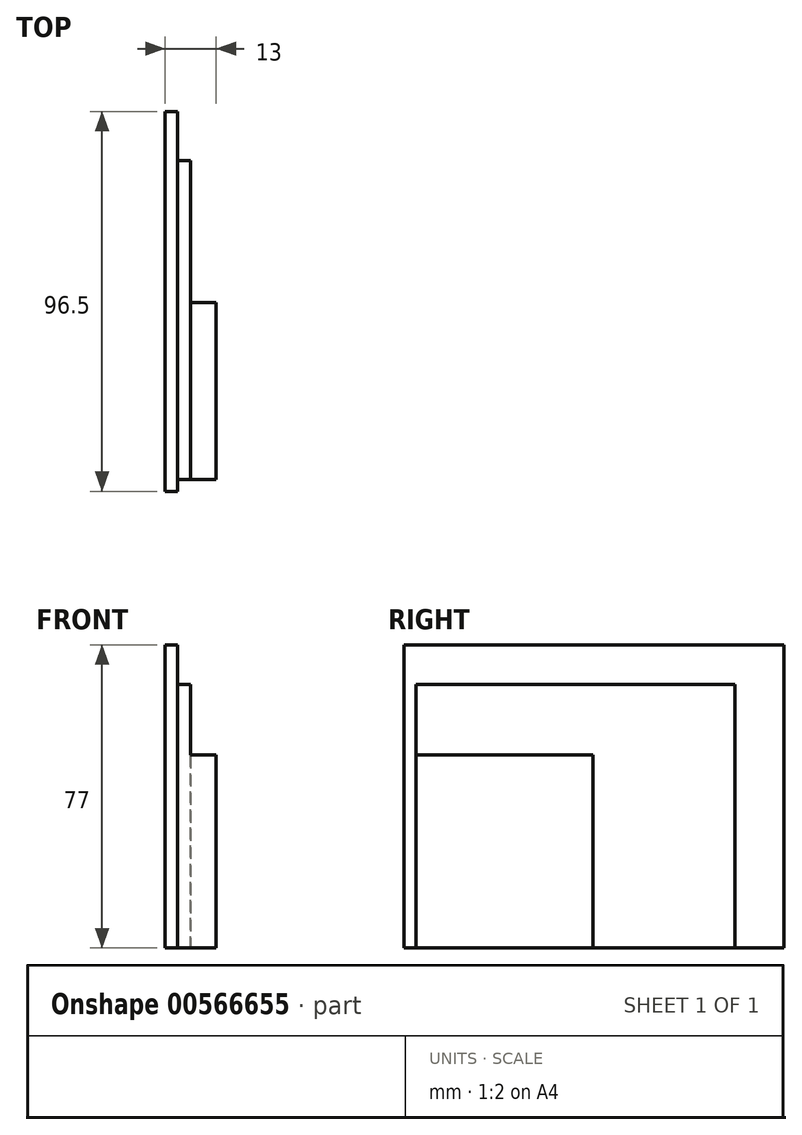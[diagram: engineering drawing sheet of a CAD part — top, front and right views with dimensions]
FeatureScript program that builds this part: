
annotation { "Feature Type Name" : "Feature", "Feature Type Description" : "" }
export const myFeature = defineFeature(function(context is Context, id is Id, definition is map)
    precondition{}
    {
        {
            var Q0;
            Q0=qCreatedBy(makeId("Right.planeOp"),FACE);
            var sketch = newSketch(context, id + "F0", { "sketchPlane" : qUnion([Q0])});
            skLineSegment(sketch, "E0.bottom", {"start": v(-48.25, 38.5) * mm, "end": v(48.25, 38.5) * mm});
            skLineSegment(sketch, "E0.top", {"start": v(-48.25, -38.5) * mm, "end": v(48.25, -38.5) * mm});
            skLineSegment(sketch, "E0.left", {"start": v(-48.25, 38.5) * mm, "end": v(-48.25, -38.5) * mm});
            skLineSegment(sketch, "E0.right", {"start": v(48.25, 38.5) * mm, "end": v(48.25, -38.5) * mm});
            skPoint(sketch, "E0.middle", {"position": v(0, 0) * mm});
            skSolve(sketch);
        }
        {
            var Q0;
            Q0=qSketchRegion(id+"F0",true);
            extrude(context, id + "F1", {"entities" : qUnion([Q0]), "endBound" : BoundingType.SYMMETRIC, "depth" : 3.2 * mm, "offsetDistance" : 25 * mm});
        }
        {
            var Q0;
            Q0=makeQuery(id+"F1.opExtrude","CAP_FACE",FACE,{"disambiguationData":[OSD([sQuery(id+"F0.wireOp",EDGE,"E0.bottom"),sQuery(id+"F0.wireOp",EDGE,"E0.top"),sQuery(id+"F0.wireOp",EDGE,"E0.left"),sQuery(id+"F0.wireOp",EDGE,"E0.right")])],"isStart":false});
            var sketch = newSketch(context, id + "F2", { "sketchPlane" : qUnion([Q0])});
            skLineSegment(sketch, "E1.bottom", {"start": v(-45.25, 28.5) * mm, "end": v(35.75, 28.5) * mm});
            skLineSegment(sketch, "E1.top", {"start": v(-45.25, -38.5) * mm, "end": v(35.75, -38.5) * mm});
            skLineSegment(sketch, "E1.left", {"start": v(-45.25, 28.5) * mm, "end": v(-45.25, -38.5) * mm});
            skLineSegment(sketch, "E1.right", {"start": v(35.75, 28.5) * mm, "end": v(35.75, -38.5) * mm});
            skSolve(sketch);
        }
        {
            var Q0;
            Q0=makeQuery(id+"F2.imprint","IMPRINT",FACE,{"disambiguationData":[TD([[makeQuery(id+"F2.imprint","IMPRINT",EDGE,{"derivedFrom":sQuery(id+"F2.wireOp",EDGE,"E1.bottom")}),-1.0]])]});
            extrude(context, id + "F3", {"entities" : qUnion([Q0]), "operationType" : NewBodyOperationType.ADD, "depth" : 3.3 * mm, "offsetDistance" : 25 * mm});
        }
        {
            var Q0;
            Q0=makeQuery(id+"F3.opExtrude","CAP_FACE",FACE,{"disambiguationData":[OSD([sQuery(id+"F2.wireOp",EDGE,"E1.bottom"),sQuery(id+"F2.wireOp",EDGE,"E1.top"),sQuery(id+"F2.wireOp",EDGE,"E1.left"),sQuery(id+"F2.wireOp",EDGE,"E1.right")])],"isStart":false});
            var sketch = newSketch(context, id + "F4", { "sketchPlane" : qUnion([Q0])});
            skLineSegment(sketch, "E2.bottom", {"start": v(-45.25, -38.5) * mm, "end": v(-0.25, -38.5) * mm});
            skLineSegment(sketch, "E2.top", {"start": v(-45.25, 10.5) * mm, "end": v(-0.25, 10.5) * mm});
            skLineSegment(sketch, "E2.left", {"start": v(-45.25, -38.5) * mm, "end": v(-45.25, 10.5) * mm});
            skLineSegment(sketch, "E2.right", {"start": v(-0.25, -38.5) * mm, "end": v(-0.25, 10.5) * mm});
            skSolve(sketch);
        }
        {
            var Q0;
            Q0=qSketchRegion(id+"F4",true);
            extrude(context, id + "F5", {"entities" : qUnion([Q0]), "operationType" : NewBodyOperationType.ADD, "depth" : 6.5 * mm, "offsetDistance" : 25 * mm});
        }
    });
